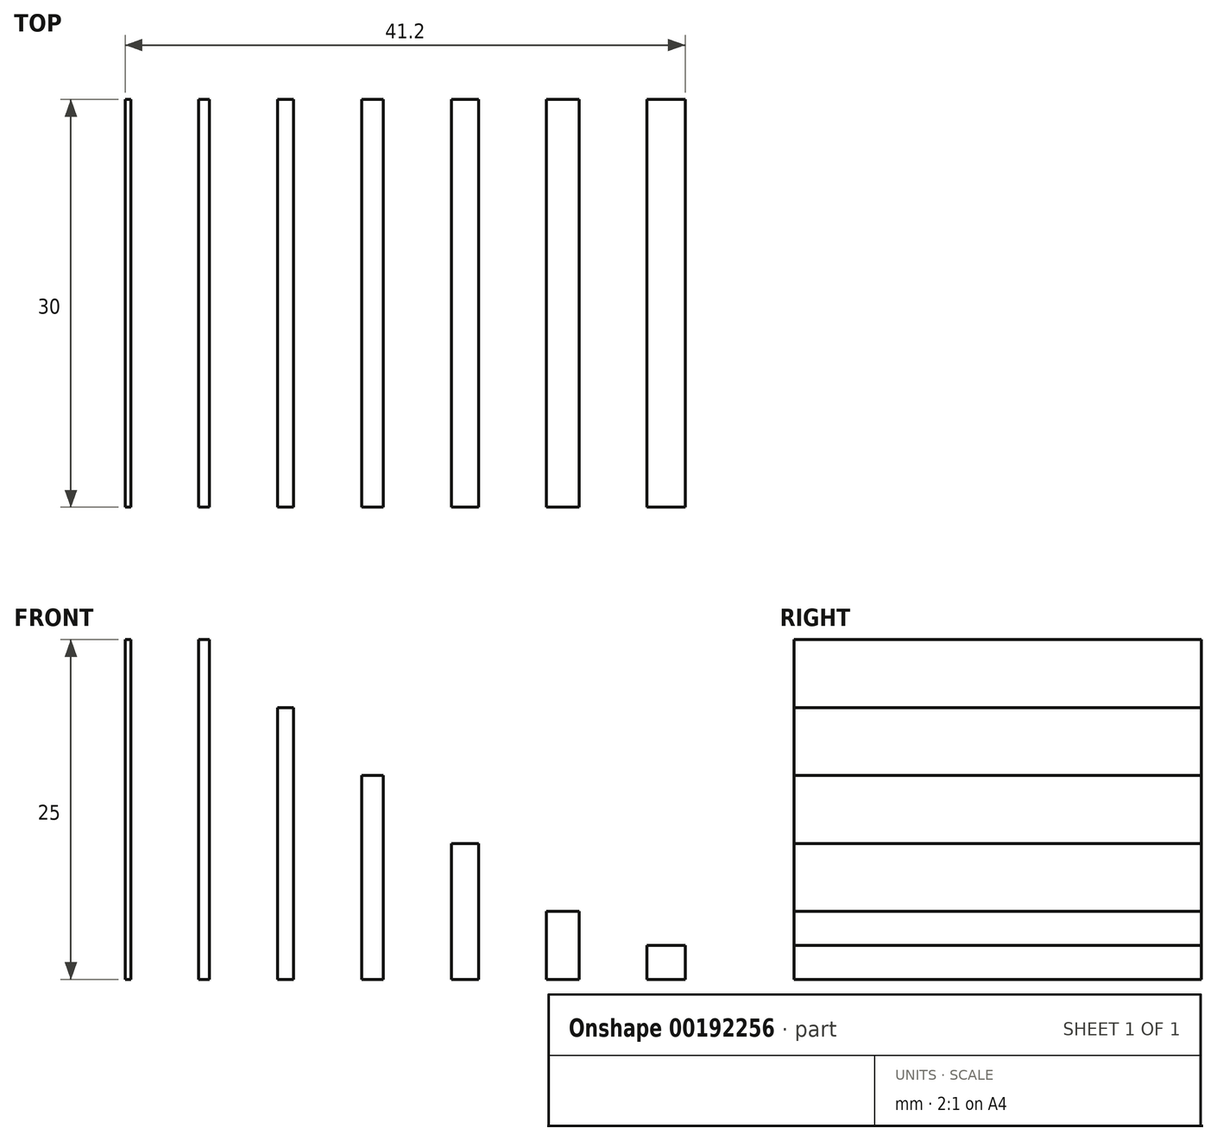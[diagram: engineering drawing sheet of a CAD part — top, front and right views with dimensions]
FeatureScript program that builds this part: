
annotation { "Feature Type Name" : "Feature", "Feature Type Description" : "" }
export const myFeature = defineFeature(function(context is Context, id is Id, definition is map)
    precondition{}
    {
        {
            var Q0;
            Q0=qCreatedBy(makeId("Top.planeOp"),FACE);
            var sketch = newSketch(context, id + "F0", { "sketchPlane" : qUnion([Q0])});
            skLineSegment(sketch, "E0.bottom", {"start": v(-41.2, 30) * mm, "end": v(0, 30) * mm});
            skLineSegment(sketch, "E0.top", {"start": v(-41.2, 0) * mm, "end": v(0, 0) * mm});
            skLineSegment(sketch, "E0.right", {"start": v(-41.2, 30) * mm, "end": v(-41.2, 0) * mm});
            skLineSegment(sketch, "E1", {"start": v(-40.8, 0) * mm, "end": v(-40.8, 30) * mm});
            skLineSegment(sketch, "E2", {"start": v(-30, 30) * mm, "end": v(-30, 0) * mm});
            skLineSegment(sketch, "E3", {"start": v(-28.8, 30) * mm, "end": v(-28.8, 0) * mm});
            skLineSegment(sketch, "E4.1.0.0", {"start": v(-17.2, 30) * mm, "end": v(-17.2, 0) * mm});
            skLineSegment(sketch, "E4.2.0.0", {"start": v(-15.2, 30) * mm, "end": v(-15.2, 0) * mm});
            skLineSegment(sketch, "E4.3.0.0", {"start": v(-35.8, 30) * mm, "end": v(-35.8, 0) * mm});
            skLineSegment(sketch, "E4.4.0.0", {"start": v(-35, 30) * mm, "end": v(-35, 0) * mm});
            skLineSegment(sketch, "E4.5.0.0", {"start": v(-23.8, 30) * mm, "end": v(-23.8, 0) * mm});
            skLineSegment(sketch, "E4.6.0.0", {"start": v(-22.2, 30) * mm, "end": v(-22.2, 0) * mm});
            skLineSegment(sketch, "E4.7.0.0", {"start": v(-10.2, 30) * mm, "end": v(-10.2, 0) * mm});
            skLineSegment(sketch, "E4.8.0.0", {"start": v(-7.8, 30) * mm, "end": v(-7.8, 0) * mm});
            skLineSegment(sketch, "E4.direction1", {"start": v(-28.8, 0) * mm, "end": v(-17.2, 0) * mm, "construction": true});
            skLineSegment(sketch, "E5", {"start": v(-2.8, 30) * mm, "end": v(-2.8, 0) * mm});
            skLineSegment(sketch, "E6", {"start": v(0, 30) * mm, "end": v(0, 0) * mm});
            skSolve(sketch);
        }
        {
            var Q0;
            {var subQ0=sQuery(id+"F0.wireOp",EDGE,"E0.right");Q0=makeQuery(id+"F0.imprint","IMPRINT",FACE,{"disambiguationData":[TD([[makeQuery(id+"F0.imprint","IMPRINT",EDGE,{"derivedFrom":subQ0}),1.0]])]});}
            extrude(context, id + "F1", {"entities" : qUnion([Q0]), "depth" : 25 * mm});
        }
        {
            var Q0;
            {var subQ0=sQuery(id+"F0.wireOp",EDGE,"E4.3.0.0");Q0=makeQuery(id+"F0.imprint","IMPRINT",FACE,{"disambiguationData":[TD([[makeQuery(id+"F0.imprint","IMPRINT",EDGE,{"derivedFrom":subQ0}),1.0]])]});}
            extrude(context, id + "F2", {"entities" : qUnion([Q0]), "depth" : 25 * mm});
        }
        {
            var Q0;
            {var subQ0=sQuery(id+"F0.wireOp",EDGE,"E2");Q0=makeQuery(id+"F0.imprint","IMPRINT",FACE,{"disambiguationData":[TD([[makeQuery(id+"F0.imprint","IMPRINT",EDGE,{"derivedFrom":subQ0}),1.0]])]});}
            extrude(context, id + "F3", {"entities" : qUnion([Q0]), "depth" : 20 * mm});
        }
        {
            var Q0;
            {var subQ0=sQuery(id+"F0.wireOp",EDGE,"E4.5.0.0");Q0=makeQuery(id+"F0.imprint","IMPRINT",FACE,{"disambiguationData":[TD([[makeQuery(id+"F0.imprint","IMPRINT",EDGE,{"derivedFrom":subQ0}),1.0]])]});}
            extrude(context, id + "F4", {"entities" : qUnion([Q0]), "depth" : 15 * mm});
        }
        {
            var Q0;
            {var subQ0=sQuery(id+"F0.wireOp",EDGE,"E4.1.0.0");Q0=makeQuery(id+"F0.imprint","IMPRINT",FACE,{"disambiguationData":[TD([[makeQuery(id+"F0.imprint","IMPRINT",EDGE,{"derivedFrom":subQ0}),1.0]])]});}
            extrude(context, id + "F5", {"entities" : qUnion([Q0]), "depth" : 10 * mm});
        }
        {
            var Q0;
            {var subQ0=sQuery(id+"F0.wireOp",EDGE,"E4.7.0.0");Q0=makeQuery(id+"F0.imprint","IMPRINT",FACE,{"disambiguationData":[TD([[makeQuery(id+"F0.imprint","IMPRINT",EDGE,{"derivedFrom":subQ0}),1.0]])]});}
            extrude(context, id + "F6", {"entities" : qUnion([Q0]), "depth" : 5 * mm});
        }
        {
            var Q0;
            {var subQ2=sQuery(id+"F0.wireOp",EDGE,"E5");Q0=makeQuery(id+"F0.imprint","IMPRINT",FACE,{"disambiguationData":[TD([[makeQuery(id+"F0.imprint","IMPRINT",EDGE,{"derivedFrom":subQ2}),1.0]])]});}
            extrude(context, id + "F7", {"entities" : qUnion([Q0]), "depth" : 2.5 * mm});
        }
    });
